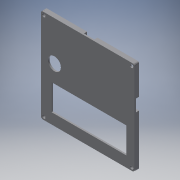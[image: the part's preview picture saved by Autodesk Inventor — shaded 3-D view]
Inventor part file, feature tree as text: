
AUTODESK INVENTOR PART (.ipt)
format: ipt  version: 2019 (Build 230136000, 136)  size: 175,616 bytes
history: native  units: mm
features: reference x7, other x4, extrude x3, sketch x3, fillet x1
ambient origin geometry x8: Origin, YZ Plane, XZ Plane, XY Plane, X Axis, Y Axis, Z Axis, Center Point
bodies: Solid1 (feature_tree)
feature tree (18):
  extrude  "Extrusion1"  Depth=90.0mm
  fillet  "Fillet1"  Radius=72.0mm
  extrude  "Extrusion2"  Depth=7.5mm
  extrude  "Extrusion3"  Depth=3.0mm
  sketch  "Sketch1"  dims[d0=90.0mm d1=90.0mm d2=72.0mm]
  reference  "Reference1"
  sketch  "Sketch2"  dims[d3=25.0mm d4=7.5mm]
  reference  "Reference2"
  reference  "Reference3"
  reference  "Reference4"
  reference  "Reference5"
  sketch  "Sketch3"  dims[d5=5.0mm d6=12.5mm d9=1.5mm d10=0.0mm d11=2.0mm d12=3.3mm d13=3.3mm d14=3.3mm d15=3.3mm d16=3.0mm d17=0.0mm d19=38.0mm d20=13.0mm d30=3.0mm d31=0.0mm]
  reference  "Reference6"
  reference  "Reference7"
  other  "<userpath>\Desktop\not_drawing_sys\cad\Assembly1.iam"
  other  "Assembly1.iam"
  other  "base:1"
  other  "<userpath>\Desktop\project\not_drawing_sys_2.0\cad\Assembly1.iam"
